# Revit family: Kessel 770100R en
name_source: partatom
category: Pipe Accessories
revit_build: Autodesk Revit Architecture 2014 (Build: 20130308_1515(x64)
units: mm (PartAtom-declared; Revit-internal decimal feet)

## types (1)
- Kessel 770100R en
    <1.010.00.2> Number of the part of the guideline = 38
    <1.010.00.3> Issue date (month) of the guideline = 201805
    <1.010.00.4> Manufacturer name = Kessel
    <1.010.00.5> Revision date of the file = 20190228
    <1.800.00.3> BS number = 100004000000000000000000000003000000???00000000012???00001
    <1.800.00.4> Comment field = StaufixControl backwater valve DN 100, exposed, Type 2 R
    <1.810.00.3> Manufacturer’s reference number = 770100R
    <1.810.00.4> DATANORM number = 770100R
    <1.810.00.6> GTIN number = 4026092076682
    <1.960/3L.00.8> Link (URL) = http://www.kessel.de
    <38.100.00.4> Drain type for floor, roof and sanitary objects = Backwater valves
    <38.110.00.4> Floor, roof and sanitary works sequences = StaufixControl backwater valve
    <38.400.00.3> Material of the drain body = polymer
    <38.700.00.15> Connection to GLT, GA = yes
    <38.700.00.16> Fire resistance class can be retrofitted = no
    <38.700.00.4> product name = StaufixControl backwater valve DN 100, exposed, Type 2 R
    <38.700.00.6> Complete article (one-piece) from combination (multi-part design) Drain body and attachment piece = yes
    <38.700.00.7> Potential compensation (ground connection) available = no
    <38.700.00.8> Electrical connection = no
    <38.710.01.10> depth [mm] = 167
    <38.710.01.11> installation height [mm] = 230
    <38.710.01.14> with sound decoupling = no
    <38.710.01.15> Leafy / Kiefang = no
    <38.710.01.3> Product name = StaufixControl backwater valve DN 100, exposed, Type 2 R
    <38.710.01.4> Type = other
    <38.710.01.5> Nominal system = DN
    <38.710.01.6> Nominal dimensions = 100
    <38.710.01.9> installation width [mm] = 389
    <38.710.13.3> Product name = StaufixControl backwater valve DN 100, exposed, Type 2 R
    <38.710.13.4> Variant of the drainage drain = point drain
    <38.710.13.7> Leafy / Kiefang = no
    <38.710.16.3> Type of measurements = external dimensions
    <38.710.16.4> Length = 389
    <38.710.16.5> Width = 167
    <38.710.16.6> Height = 230
    CONNECTOR0_DIAMETER_dX_0r = 0 mm  [stored 0 ft]
    CONNECTOR0_dX_01 = 15 mm  [stored 0.0492126 ft]
    CONNECTOR0_ref_dX = 15 mm  [stored 0.0492126 ft]
    CONNECTOR1_DIAMETER_dX_0r = 0 mm  [stored 0 ft]
    CONNECTOR1_dX_00 = 326 mm
    CONNECTOR1_dX_01 = 386 mm
    CONNECTOR1_ref_dX = 326 mm
    CONNECTOR1_ref_dZ = 8 mm  [stored 0.0262467 ft]
    Manufacturer = Kessel
    Model = 770100R
    URL = www.kessel.com

note: [stored X ft] marks values corroborated as IEEE doubles in the binary element streams (Revit-internal decimal feet)
